# Revit family: Windows_Roof-Windows_Lamilux_F100_Round-Rooflight-Dome_Decke
name_source: partatom
category: Fenster
units: mm (PartAtom-declared; Revit-internal decimal feet)

## family parameters
Basisbauteil = Geschossdecke
Beim Laden mit Abzugskörper schneiden = Ja
Gemeinsam genutzt = Nein
Immer vertikal = Ja
Raumberechnungspunkt = Nein

## types (21) — shared parameters
BIMobject categroy = Roof Windows
Baugruppenkennzeichen = B3020110
Brand URL = https://www.lamilux.de
Date of publishing = 2020-04-27
Design country = Germany
Edition number = 1
Hersteller = LAMILUX Heinrich Strunz GmbH
IFC Classification = Window
Main Material = Lamilux-White
Manufacturer country = Germany
Manufacturer name = LAMILUX
Material Main = Plastic
Material secondary = Plastic
NBS Reference Code = 20-30-74
NBS Reference Description = Roof Light Systems
OmniClass Code = 23-17 17 00
OmniClass Description = Skylights
Opening types = Ventilable, fixed
Option 1 = Glazing : Double glazing
Option 10 = Material : PETG + PC16
Option 11 = Mid Glazing : Clear
Option 12 = Internal Glazing : Clear
Option 13 = Internal Glazing : Opal
Option 14 = Internal Glazing : PC16 clear
Option 15 = Internal Glazing : PC16 opal
Option 16 = Mid Glazing : Opal
Option 17 = Mid Glazing : None
Option 2 = Glazing : Triple glazing
Option 3 = Glazing : Double glazing+PC16
Option 4 = External Glazing : Clear
Option 5 = External Glazing : Opal
Option 6 = External Glazing : Heatstop
Option 7 = Material : SAN
Option 8 = Material : PETG
Option 9 = Material : SAN + PC16
Product SKU = Lamilux_F100_round_rooflight_dome
Product family = Daylight element
Product group = Flat roof window
QR code = https://www.bimobject.com
Secondary Material = Lamilux- Glass
UNSPSC Code = 301516
URL = https://www.lamilux.de
Uniclass 1.4 Code = JL11
Uniclass 1.4 Description = Rooflights/Roof windows
Uniclass 2.0 Code = SS-20-30-74
Uniclass 2.0 Description = Roof Light Systems
Uniclass 2015 Code = Ss_30_30_34
Uniclass 2015 Name = Glass unite masonry roof light systems
zero-valued in all types: Weight Net (kg)

## per-type parameters (varying)
| type | Breite | Höhe | Internal Radius | Nominal hight | Nominal width | Rohbauhöhe |
| 100x30 | 1000 mm  [stored 3.28084 ft] | 300 mm  [stored 0.984252 ft] | 500 mm  [stored 1.64042 ft] | 300 mm  [stored 0.984252 ft] | 1000 mm  [stored 3.28084 ft] | 300 mm  [stored 0.984252 ft] |
| 100x50 | 1000 mm  [stored 3.28084 ft] | 500 mm  [stored 1.64042 ft] | 500 mm  [stored 1.64042 ft] | 500 mm  [stored 1.64042 ft] | 1000 mm  [stored 3.28084 ft] | 500 mm  [stored 1.64042 ft] |
| 100x70 | 1000 mm  [stored 3.28084 ft] | 700 mm  [stored 2.29659 ft] | 500 mm  [stored 1.64042 ft] | 700 mm  [stored 2.29659 ft] | 1000 mm  [stored 3.28084 ft] | 700 mm  [stored 2.29659 ft] |
| 120x30 | 1200 mm | 300 mm  [stored 0.984252 ft] | 600 mm | 300 mm  [stored 0.984252 ft] | 1200 mm | 300 mm  [stored 0.984252 ft] |
| 120x50 | 1200 mm | 500 mm  [stored 1.64042 ft] | 600 mm | 500 mm  [stored 1.64042 ft] | 1200 mm | 500 mm  [stored 1.64042 ft] |
| 120x70 | 1200 mm | 700 mm  [stored 2.29659 ft] | 600 mm | 700 mm  [stored 2.29659 ft] | 1200 mm | 700 mm  [stored 2.29659 ft] |
| 150x30 | 1500 mm  [stored 4.92126 ft] | 300 mm  [stored 0.984252 ft] | 750 mm  [stored 2.46063 ft] | 300 mm  [stored 0.984252 ft] | 1500 mm  [stored 4.92126 ft] | 300 mm  [stored 0.984252 ft] |
| 150x50 | 1500 mm  [stored 4.92126 ft] | 500 mm  [stored 1.64042 ft] | 750 mm  [stored 2.46063 ft] | 500 mm  [stored 1.64042 ft] | 1500 mm  [stored 4.92126 ft] | 500 mm  [stored 1.64042 ft] |
| 150x70 | 1500 mm  [stored 4.92126 ft] | 700 mm  [stored 2.29659 ft] | 750 mm  [stored 2.46063 ft] | 700 mm  [stored 2.29659 ft] | 1500 mm  [stored 4.92126 ft] | 700 mm  [stored 2.29659 ft] |
| 180x30 | 1800 mm  [stored 5.90551 ft] | 300 mm  [stored 0.984252 ft] | 900 mm  [stored 2.95276 ft] | 300 mm  [stored 0.984252 ft] | 1800 mm  [stored 5.90551 ft] | 300 mm  [stored 0.984252 ft] |
| 180x50 | 1800 mm  [stored 5.90551 ft] | 500 mm  [stored 1.64042 ft] | 900 mm  [stored 2.95276 ft] | 500 mm  [stored 1.64042 ft] | 1800 mm  [stored 5.90551 ft] | 500 mm  [stored 1.64042 ft] |
| 180x70 | 1800 mm  [stored 5.90551 ft] | 700 mm  [stored 2.29659 ft] | 900 mm  [stored 2.95276 ft] | 700 mm  [stored 2.29659 ft] | 1800 mm  [stored 5.90551 ft] | 700 mm  [stored 2.29659 ft] |
| 60x30 | 600 mm | 300 mm  [stored 0.984252 ft] | 300 mm  [stored 0.984252 ft] | 300 mm  [stored 0.984252 ft] | 600 mm | 300 mm  [stored 0.984252 ft] |
| 60x50 | 600 mm | 500 mm  [stored 1.64042 ft] | 300 mm  [stored 0.984252 ft] | 500 mm  [stored 1.64042 ft] | 600 mm | 500 mm  [stored 1.64042 ft] |
| 60x70 | 600 mm | 700 mm  [stored 2.29659 ft] | 300 mm  [stored 0.984252 ft] | 700 mm  [stored 2.29659 ft] | 600 mm | 700 mm  [stored 2.29659 ft] |
| 80x30 | 800 mm  [stored 2.62467 ft] | 300 mm  [stored 0.984252 ft] | 400 mm  [stored 1.31234 ft] | 300 mm  [stored 0.984252 ft] | 800 mm  [stored 2.62467 ft] | 300 mm  [stored 0.984252 ft] |
| 80x50 | 800 mm  [stored 2.62467 ft] | 500 mm  [stored 1.64042 ft] | 400 mm  [stored 1.31234 ft] | 500 mm  [stored 1.64042 ft] | 800 mm  [stored 2.62467 ft] | 500 mm  [stored 1.64042 ft] |
| 80x70 | 800 mm  [stored 2.62467 ft] | 700 mm  [stored 2.29659 ft] | 400 mm  [stored 1.31234 ft] | 700 mm  [stored 2.29659 ft] | 800 mm  [stored 2.62467 ft] | 700 mm  [stored 2.29659 ft] |
| 90x30 | 900 mm  [stored 2.95276 ft] | 300 mm  [stored 0.984252 ft] | 450 mm  [stored 1.47638 ft] | 300 mm  [stored 0.984252 ft] | 900 mm  [stored 2.95276 ft] | 300 mm  [stored 0.984252 ft] |
| 90x50 | 900 mm  [stored 2.95276 ft] | 500 mm  [stored 1.64042 ft] | 450 mm  [stored 1.47638 ft] | 500 mm  [stored 1.64042 ft] | 900 mm  [stored 2.95276 ft] | 500 mm  [stored 1.64042 ft] |
| 90x70 | 900 mm  [stored 2.95276 ft] | 700 mm  [stored 2.29659 ft] | 450 mm  [stored 1.47638 ft] | 700 mm  [stored 2.29659 ft] | 900 mm  [stored 2.95276 ft] | 700 mm  [stored 2.29659 ft] |

note: [stored X ft] marks values corroborated as IEEE doubles in the binary element streams (Revit-internal decimal feet)

## geometry (parser evidence)
native form markers: Sweep x16
no freeform markers — native parametric forms only
